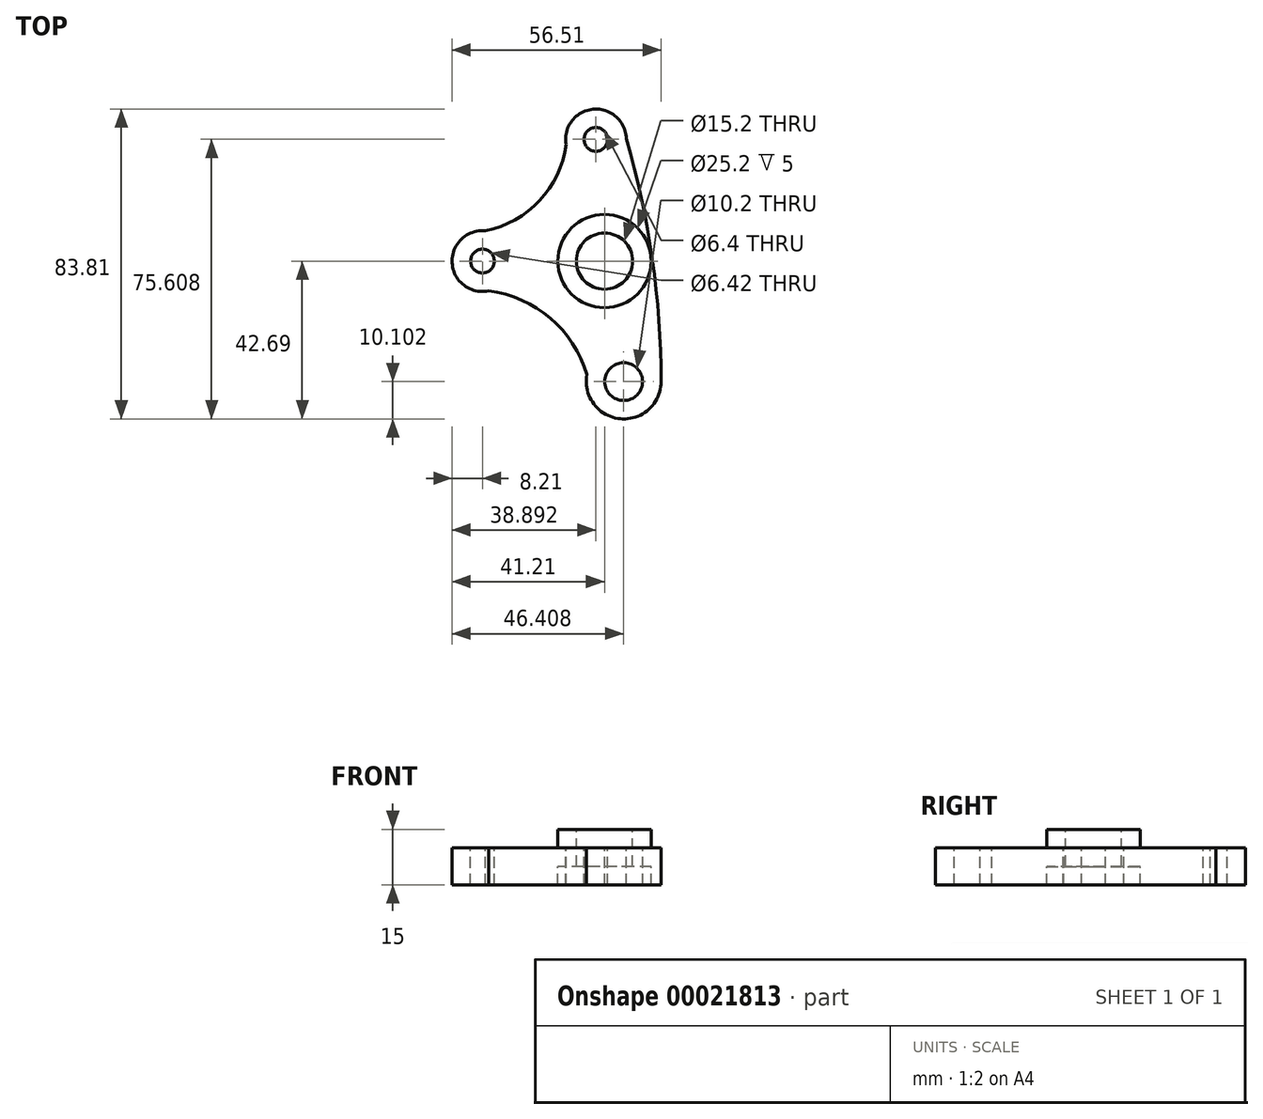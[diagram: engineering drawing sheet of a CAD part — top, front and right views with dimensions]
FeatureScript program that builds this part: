
annotation { "Feature Type Name" : "Feature", "Feature Type Description" : "" }
export const myFeature = defineFeature(function(context is Context, id is Id, definition is map)
    precondition{}
    {
        {
            var Q0;
            Q0=qCreatedBy(makeId("Top.planeOp"),FACE);
            var sketch = newSketch(context, id + "F0", { "sketchPlane" : qUnion([Q0])});
            skCircle(sketch, "E0", {"center": v(0, 0) * mm, "radius": 7.6 * mm});
            skCircle(sketch, "E1", {"center": v(5.2, -32.59) * mm, "radius": 5.1 * mm});
            skCircle(sketch, "E2", {"center": v(-33, 0) * mm, "radius": 3.21 * mm});
            skCircle(sketch, "E3", {"center": v(-2.32, 32.92) * mm, "radius": 3.2 * mm});
            skArc(sketch, "E4.0", {"start": v(0.72, 25.3) * mm, "mid": v(-2.9, 41.1) * mm, "end": v(-4.26, 24.95) * mm});
            skArc(sketch, "E5.0", {"start": v(-25.18, 2.5) * mm, "mid": v(-41.21, 0) * mm, "end": v(-25.18, -2.5) * mm});
            skArc(sketch, "E6.0", {"start": v(1.19, -23.32) * mm, "mid": v(6.79, -42.56) * mm, "end": v(6.13, -22.53) * mm});
            skArc(sketch, "E7", {"start": v(-32.22, 8.17) * mm, "mid": v(-17.55, 16.37) * mm, "end": v(-10.4, 31.57) * mm});
            skArc(sketch, "E8", {"start": v(-4.72, -30.7) * mm, "mid": v(-14.67, -15.46) * mm, "end": v(-31.29, -8.03) * mm});
            skArc(sketch, "E9", {"start": v(15.3, -32.59) * mm, "mid": v(12.94, 0.57) * mm, "end": v(5.88, 33.05) * mm});
            skArc(sketch, "E10.trimOffspring", {"start": v(-11.37, -5.43) * mm, "mid": v(-8.05, -9.7) * mm, "end": v(-3.26, -12.17) * mm});
            skArc(sketch, "E11.trimOffspring", {"start": v(6.92, -10.53) * mm, "mid": v(12.53, 1.3) * mm, "end": v(4.62, 11.72) * mm});
            skLineSegment(sketch, "E12", {"start": v(0.72, 25.3) * mm, "end": v(4.62, 11.72) * mm});
            skLineSegment(sketch, "E13", {"start": v(-4.26, 24.95) * mm, "end": v(-6.41, 10.85) * mm});
            skLineSegment(sketch, "E14", {"start": v(-25.18, 2.5) * mm, "end": v(-11.35, 5.47) * mm});
            skLineSegment(sketch, "E15", {"start": v(-25.18, -2.5) * mm, "end": v(-11.37, -5.43) * mm});
            skLineSegment(sketch, "E16", {"start": v(6.13, -22.53) * mm, "end": v(6.92, -10.53) * mm});
            skLineSegment(sketch, "E17", {"start": v(1.19, -23.32) * mm, "end": v(-3.26, -12.17) * mm});
            skCircle(sketch, "E18.converted", {"center": v(0, 0) * mm, "radius": 12.6 * mm});
            skSolve(sketch);
        }
        {
            var Q0;
            Q0=makeQuery(id+"F0.imprint","IMPRINT",FACE,{"disambiguationData":[TD([[makeQuery(id+"F0.imprint","IMPRINT",EDGE,{"derivedFrom":sQuery(id+"F0.wireOp",EDGE,"E0")}),-1.0]])]});
            var Q1;
            {var subQ1=sQuery(id+"F0.wireOp",EDGE,"E9");Q1=makeQuery(id+"F0.imprint","IMPRINT",FACE,{"disambiguationData":[TD([[makeQuery(id+"F0.imprint","IMPRINT",EDGE,{"derivedFrom":subQ1}),1.0]])]});}
            var Q2;
            Q2=makeQuery(id+"F0.imprint","IMPRINT",FACE,{"disambiguationData":[TD([[makeQuery(id+"F0.imprint","IMPRINT",EDGE,{"derivedFrom":sQuery(id+"F0.wireOp",EDGE,"c4e526d3-71b7-426b-a748-584161a03861.0")}),-1.0]])]});
            var Q3;
            {var subQ2=sQuery(id+"F0.wireOp",EDGE,"E8");Q3=makeQuery(id+"F0.imprint","IMPRINT",FACE,{"disambiguationData":[TD([[makeQuery(id+"F0.imprint","IMPRINT",EDGE,{"derivedFrom":subQ2}),-1.0]])]});}
            extrude(context, id + "F1", {"entities" : qUnion([Q0, Q1, Q2, Q3]), "oppositeDirection" : true, "depth" : 5 * mm});
        }
        {
            var Q0;
            Q0=makeQuery(id+"F0.imprint","IMPRINT",FACE,{"disambiguationData":[TD([[makeQuery(id+"F0.imprint","IMPRINT",EDGE,{"derivedFrom":sQuery(id+"F0.wireOp",EDGE,"E0")}),-1.0]])]});
            extrude(context, id + "F2", {"entities" : qUnion([Q0]), "operationType" : NewBodyOperationType.ADD, "depth" : 5 * mm});
        }
        {
            var Q0;
            Q0 = qSketchRegion(id + "F0", true);
            var Q1;
            Q1=makeQuery(id+"F2.opExtrude","CAP_FACE",FACE,{"disambiguationData":[OSD([sQuery(id+"F0.wireOp",EDGE,"E0"),sQuery(id+"F0.wireOp",EDGE,"E18.converted")])],"isStart":false});
            extrude(context, id + "F3", {"entities" : qUnion([Q0, Q1]), "operationType" : NewBodyOperationType.ADD, "oppositeDirection" : true, "depth" : 10 * mm});
        }
    });
